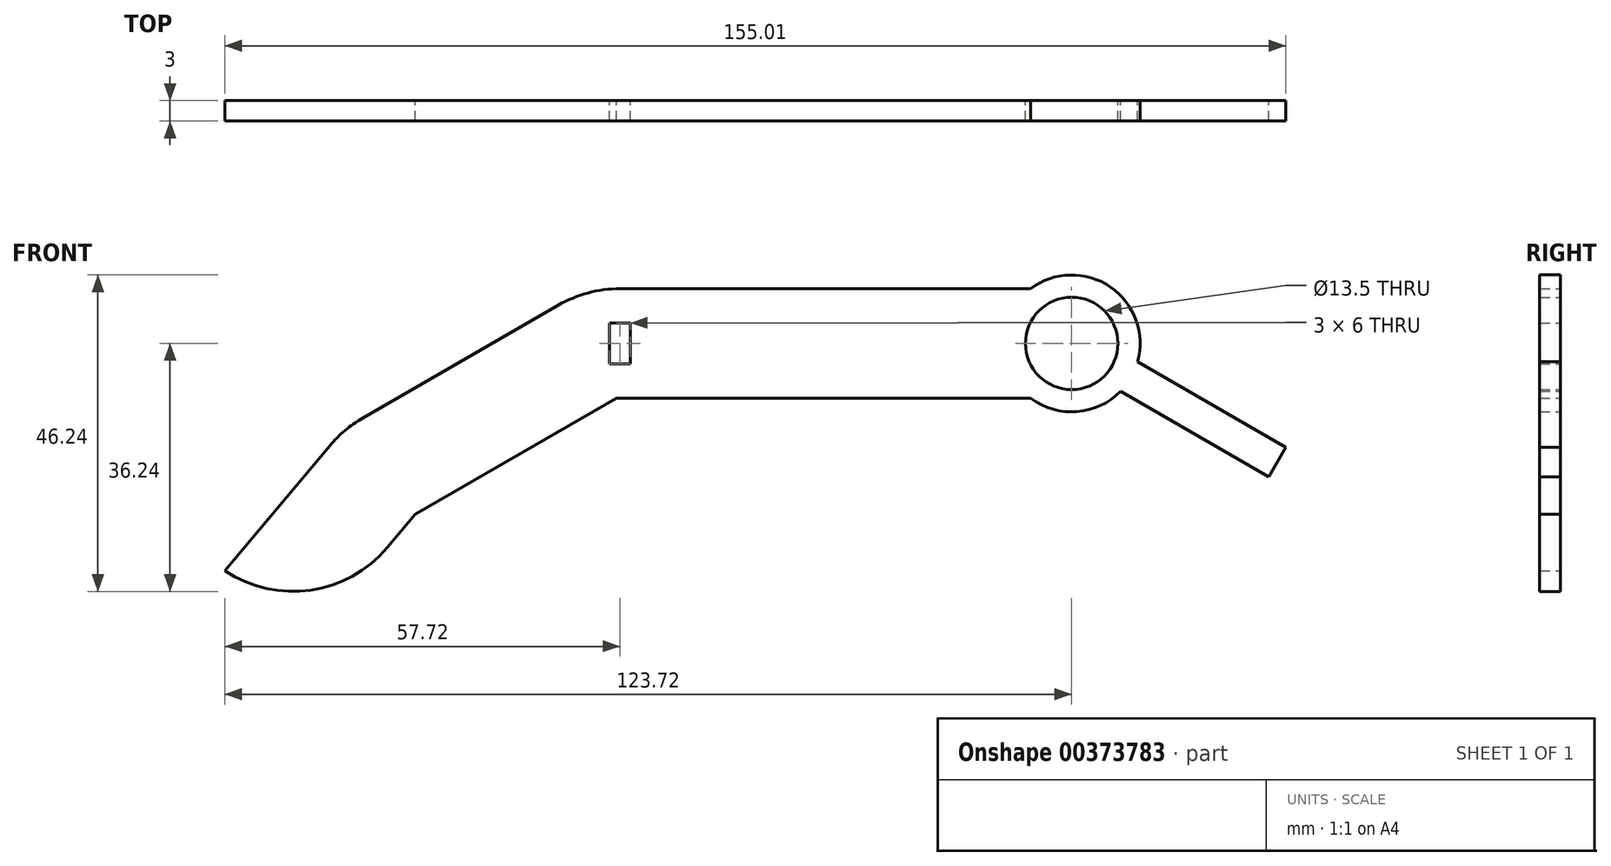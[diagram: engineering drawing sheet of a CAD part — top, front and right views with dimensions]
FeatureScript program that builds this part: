
annotation { "Feature Type Name" : "Feature", "Feature Type Description" : "" }
export const myFeature = defineFeature(function(context is Context, id is Id, definition is map)
    precondition{}
    {
        {
            var Q0;
            Q0=qCreatedBy(makeId("Front.planeOp"),FACE);
            var sketch = newSketch(context, id + "F0", { "sketchPlane" : qUnion([Q0])});
            skLineSegment(sketch, "E0.bottom", {"start": v(33, -10) * mm, "end": v(-33, -10) * mm, "construction": true});
            skLineSegment(sketch, "E0.top", {"start": v(33, 10) * mm, "end": v(-33, 10) * mm, "construction": true});
            skLineSegment(sketch, "E0.left", {"start": v(33, -10) * mm, "end": v(33, 10) * mm, "construction": true});
            skLineSegment(sketch, "E0.right", {"start": v(-33, -10) * mm, "end": v(-33, 10) * mm, "construction": true});
            skPoint(sketch, "E0.middle", {"position": v(0, 0) * mm});
            skArc(sketch, "E1", {"start": v(-33, 10) * mm, "mid": v(-38.18, 9.32) * mm, "end": v(-43, 7.32) * mm, "construction": true});
            skLineSegment(sketch, "E2", {"start": v(-43, 7.32) * mm, "end": v(-33, -10) * mm, "construction": true});
            skLineSegment(sketch, "E3", {"start": v(-43, 7.32) * mm, "end": v(-71.58, -9.18) * mm, "construction": true});
            skLineSegment(sketch, "E4", {"start": v(-33, -10) * mm, "end": v(-61.58, -26.5) * mm, "construction": true});
            skLineSegment(sketch, "E5", {"start": v(-71.58, -9.18) * mm, "end": v(-61.58, -26.5) * mm, "construction": true});
            skArc(sketch, "E6", {"start": v(-71.58, -9.18) * mm, "mid": v(-74.43, -11.18) * mm, "end": v(-76.9, -13.64) * mm, "construction": true});
            skLineSegment(sketch, "E7", {"start": v(-76.9, -13.64) * mm, "end": v(-61.58, -26.5) * mm, "construction": true});
            skLineSegment(sketch, "E8", {"start": v(-76.9, -13.64) * mm, "end": v(-93.61, -33.56) * mm, "construction": true});
            skLineSegment(sketch, "E9", {"start": v(-61.58, -26.5) * mm, "end": v(-65.44, -31.1) * mm, "construction": true});
            skArc(sketch, "E10", {"start": v(-93.61, -33.56) * mm, "mid": v(-79.01, -38.16) * mm, "end": v(-65.44, -31.1) * mm, "construction": true});
            skCircle(sketch, "E11", {"center": v(33, 0) * mm, "radius": 6.75 * mm});
            skLineSegment(sketch, "E12.0", {"start": v(33, -8) * mm, "end": v(-33.54, -8) * mm, "construction": true});
            skLineSegment(sketch, "E12.1", {"start": v(-33.54, -8) * mm, "end": v(-62.88, -24.94) * mm});
            skLineSegment(sketch, "E12.2", {"start": v(-62.88, -24.94) * mm, "end": v(-66.97, -29.81) * mm});
            skArc(sketch, "E12.3", {"start": v(-90.72, -33.23) * mm, "mid": v(-78.2, -36.06) * mm, "end": v(-66.97, -29.81) * mm});
            skLineSegment(sketch, "E12.4", {"start": v(-75.37, -14.93) * mm, "end": v(-90.72, -33.23) * mm});
            skLineSegment(sketch, "E12.5", {"start": v(33, 8) * mm, "end": v(-33, 8) * mm, "construction": true});
            skArc(sketch, "E12.6", {"start": v(-33, 8) * mm, "mid": v(-37.66, 7.39) * mm, "end": v(-42, 5.59) * mm});
            skLineSegment(sketch, "E12.7", {"start": v(-42, 5.59) * mm, "end": v(-70.58, -10.91) * mm});
            skArc(sketch, "E12.8", {"start": v(-70.58, -10.91) * mm, "mid": v(-73.15, -12.71) * mm, "end": v(-75.37, -14.93) * mm});
            skLineSegment(sketch, "E13", {"start": v(33, -8) * mm, "end": v(33, -10) * mm});
            skLineSegment(sketch, "E14", {"start": v(33, 8) * mm, "end": v(33, 10) * mm});
            skArc(sketch, "E15", {"start": v(33, -10) * mm, "mid": v(29.84, -9.49) * mm, "end": v(27, -8) * mm});
            skArc(sketch, "E16", {"start": v(33, 10) * mm, "mid": v(29.84, 9.49) * mm, "end": v(27, 8) * mm});
            skLineSegment(sketch, "E17", {"start": v(-33, 8) * mm, "end": v(27, 8) * mm});
            skLineSegment(sketch, "E18", {"start": v(27, -8) * mm, "end": v(-33.54, -8) * mm});
            skArc(sketch, "E19", {"start": v(33, 10) * mm, "mid": v(40.96, 6.05) * mm, "end": v(42.64, -2.68) * mm});
            skArc(sketch, "E20", {"start": v(33, -10) * mm, "mid": v(36.87, -9.22) * mm, "end": v(40.14, -7) * mm});
            skLineSegment(sketch, "E21", {"start": v(33, 0) * mm, "end": v(63.04, -17.34) * mm, "construction": true});
            skLineSegment(sketch, "E22", {"start": v(42.64, -2.68) * mm, "end": v(64.29, -15.18) * mm});
            skLineSegment(sketch, "E23", {"start": v(64.29, -15.18) * mm, "end": v(61.79, -19.5) * mm});
            skLineSegment(sketch, "E24", {"start": v(61.79, -19.5) * mm, "end": v(40.14, -7) * mm});
            skLineSegment(sketch, "E25.bottom", {"start": v(-31.5, -3) * mm, "end": v(-34.5, -3) * mm});
            skLineSegment(sketch, "E25.top", {"start": v(-31.5, 3) * mm, "end": v(-34.5, 3) * mm});
            skLineSegment(sketch, "E25.left", {"start": v(-31.5, -3) * mm, "end": v(-31.5, 3) * mm});
            skLineSegment(sketch, "E25.right", {"start": v(-34.5, -3) * mm, "end": v(-34.5, 3) * mm});
            skPoint(sketch, "E25.middle", {"position": v(-33, 0) * mm});
            skSolve(sketch);
        }
        {
            var Q0;
            Q0=qSketchRegion(id+"F0",true);
            extrude(context, id + "F1", {"entities" : qUnion([Q0]), "depth" : 3 * mm});
        }
    });
